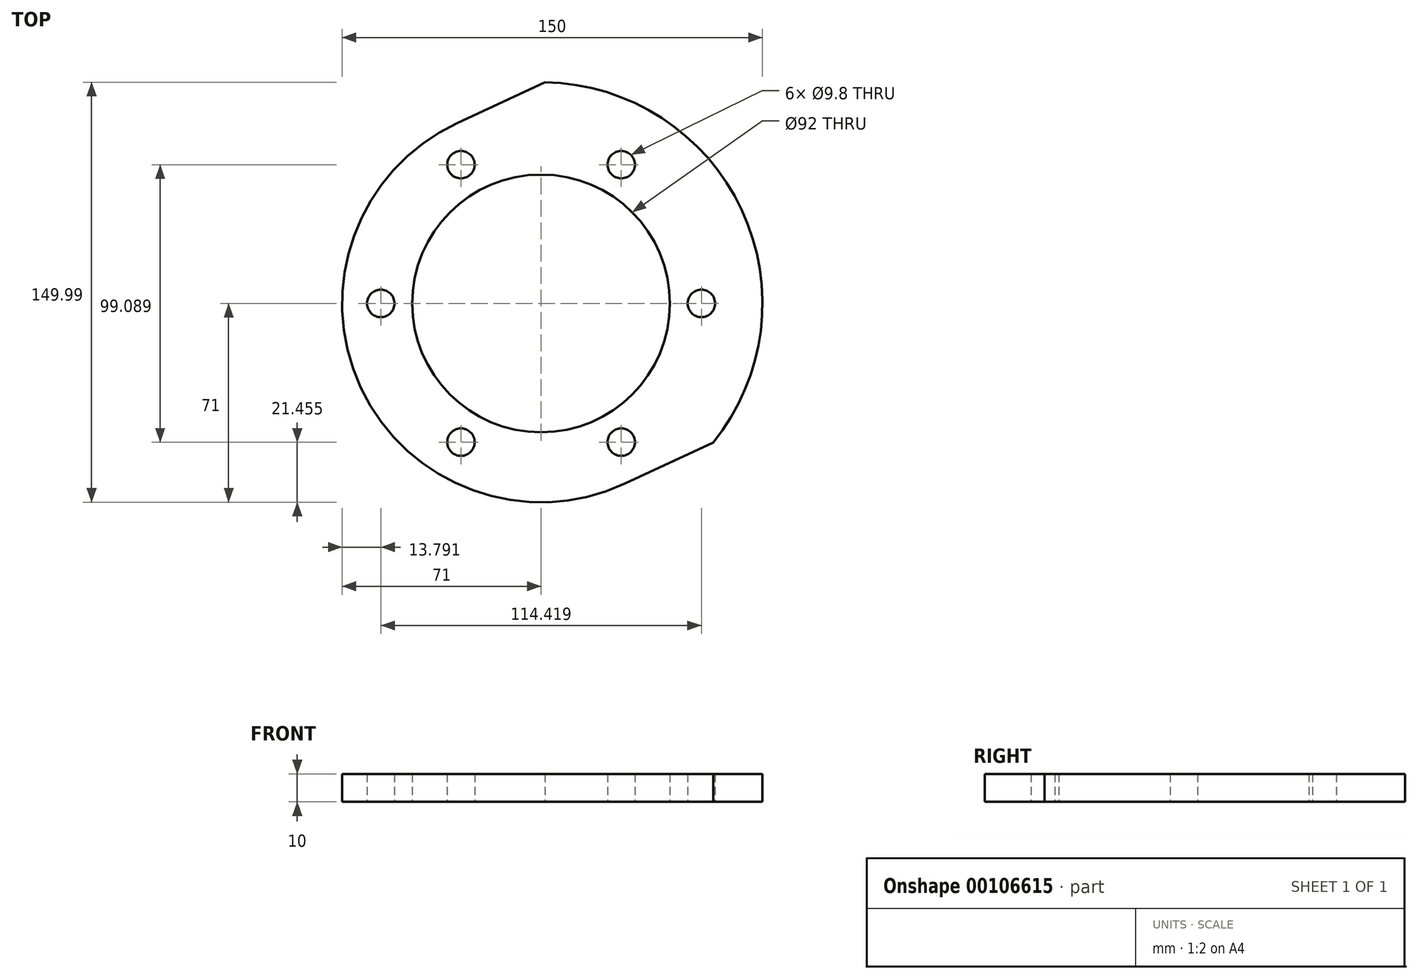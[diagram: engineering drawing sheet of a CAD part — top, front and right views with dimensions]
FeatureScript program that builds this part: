
annotation { "Feature Type Name" : "Feature", "Feature Type Description" : "" }
export const myFeature = defineFeature(function(context is Context, id is Id, definition is map)
    precondition{}
    {
        {
            var Q0;
            Q0=qCreatedBy(makeId("Top.planeOp"),FACE);
            var sketch = newSketch(context, id + "F0", { "sketchPlane" : qUnion([Q0])});
            skArc(sketch, "E0", {"start": v(-30, 64.35) * mm, "mid": v(-64.35, -30) * mm, "end": v(30, -64.35) * mm});
            skArc(sketch, "E1", {"start": v(61.4, -49.7) * mm, "mid": v(71.6, 33.39) * mm, "end": v(1.39, 78.99) * mm});
            skCircle(sketch, "E2", {"center": v(0, 0) * mm, "radius": 46 * mm});
            skLineSegment(sketch, "E3", {"start": v(-30, 64.35) * mm, "end": v(1.39, 78.99) * mm});
            skLineSegment(sketch, "E4", {"start": v(30, -64.35) * mm, "end": v(61.4, -49.7) * mm});
            skLineSegment(sketch, "E5", {"start": v(0, 0) * mm, "end": v(108.63, 0) * mm, "construction": true});
            skCircle(sketch, "E6", {"center": v(0, 0) * mm, "radius": 57.2 * mm, "construction": true});
            skCircle(sketch, "E7", {"center": v(57.2, 0) * mm, "radius": 4.9 * mm});
            skCircle(sketch, "E8.1.0", {"center": v(28.6, 49.54) * mm, "radius": 4.9 * mm});
            skCircle(sketch, "E8.2.0", {"center": v(-28.6, 49.54) * mm, "radius": 4.9 * mm});
            skCircle(sketch, "E8.3.0", {"center": v(-57.2, 0) * mm, "radius": 4.9 * mm});
            skCircle(sketch, "E8.4.0", {"center": v(-28.6, -49.54) * mm, "radius": 4.9 * mm});
            skCircle(sketch, "E8.5.0", {"center": v(28.6, -49.54) * mm, "radius": 4.9 * mm});
            skSolve(sketch);
        }
        {
            var Q0;
            Q0=makeQuery(id+"F0.imprint","IMPRINT",FACE,{"disambiguationData":[TD([[makeQuery(id+"F0.imprint","IMPRINT",EDGE,{"derivedFrom":sQuery(id+"F0.wireOp",EDGE,"E0")}),1.0]])]});
            extrude(context, id + "F1", {"entities" : qUnion([Q0]), "depth" : 10 * mm});
        }
    });
